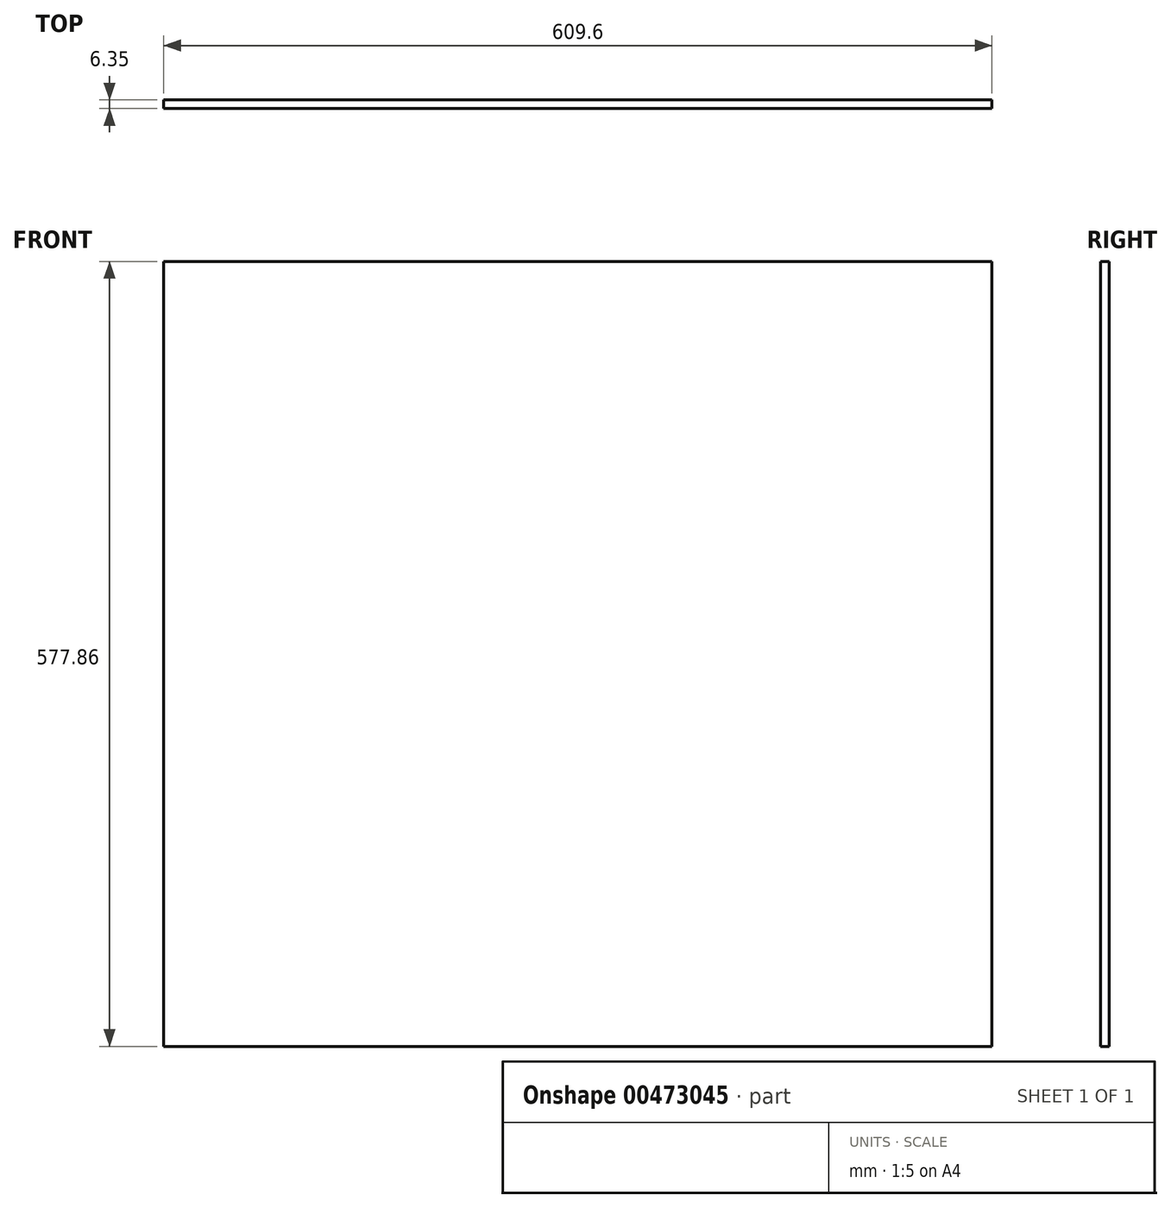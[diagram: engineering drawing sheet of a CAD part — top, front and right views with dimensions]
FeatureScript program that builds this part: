
annotation { "Feature Type Name" : "Feature", "Feature Type Description" : "" }
export const myFeature = defineFeature(function(context is Context, id is Id, definition is map)
    precondition{}
    {
        {
            var Q0;
            Q0=qCreatedBy(makeId("Front.planeOp"),FACE);
            var sketch = newSketch(context, id + "F0", { "sketchPlane" : qUnion([Q0])});
            skLineSegment(sketch, "E0.bottom", {"start": v(304.8, 288.93) * mm, "end": v(-304.8, 288.93) * mm});
            skLineSegment(sketch, "E0.top", {"start": v(304.8, -288.93) * mm, "end": v(-304.8, -288.93) * mm});
            skLineSegment(sketch, "E0.left", {"start": v(304.8, 288.93) * mm, "end": v(304.8, -288.93) * mm});
            skLineSegment(sketch, "E0.right", {"start": v(-304.8, 288.93) * mm, "end": v(-304.8, -288.93) * mm});
            skPoint(sketch, "E0.middle", {"position": v(0, 0) * mm});
            skSolve(sketch);
        }
        {
            var Q0;
            Q0 = qSketchRegion(id + "F0", true);
            var Q1;
            Q1=makeQuery(id+"F0.imprint","IMPRINT",FACE,{"disambiguationData":[TD([[makeQuery(id+"F0.imprint","IMPRINT",EDGE,{"derivedFrom":sQuery(id+"F0.wireOp",EDGE,"E0.bottom")}),1.0]])]});
            extrude(context, id + "F1", {"entities" : qUnion([Q0, Q1]), "depth" : 6.35 * mm});
        }
    });
